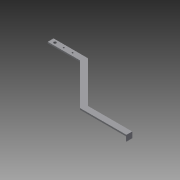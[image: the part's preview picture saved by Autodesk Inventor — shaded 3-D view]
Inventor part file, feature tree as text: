
AUTODESK INVENTOR PART (.ipt)
format: ipt  version: 2013 (Build 170138000, 138)  size: 174,080 bytes
history: native  units: in
note: dims shown in document units (in); Inventor stores cm internally (conversion verified against a paired STEP export)
features: extrude x8, sketch x8
ambient origin geometry x8: Origin, YZ Plane, XZ Plane, XY Plane, X Axis, Y Axis, Z Axis, Center Point
bodies: Solid1 (feature_tree)
feature tree (16):
  extrude  "Extrusion1"  Depth=1.0in
  extrude  "Extrusion2"  Depth=1.0in
  extrude  "Extrusion3"  Depth=9.586in
  extrude  "Extrusion5"  Depth=7.5in
  extrude  "Extrusion7"  Depth=0.25in TaperAngle=0.0deg
  extrude  "Extrusion8"  Depth=1.0in
  extrude  "Extrusion9"  Depth=1.75in TaperAngle=0.0deg
  extrude  "Extrusion10"  Depth=2.25in
  sketch  "Sketch1"  dims[d0=5.25in d1=1.0in]
  sketch  "Sketch2"  dims[d2=112.5deg d3=1.0in]
  sketch  "Sketch3"  dims[d4=135.0deg d5=9.586in]
  sketch  "Sketch6"  dims[d6=0.5in d7=7.5in]
  sketch  "Sketch8"  dims[d8=1.0in d9=0.25in d10=0.0in]
  sketch  "Sketch9"  dims[d11=1.0in d12=1.0in]
  sketch  "Sketch10"  dims[d13=0.0625in d14=0.0in d15=1.75in d16=0.0in]
  sketch  "Sketch11"  dims[d21=0.25in d22=0.0in d29=2.25in d30=1.5in d31=3.0in d32=0.0in d33=0.25in d34=0.25in d35=1.0in d36=0.0in d37=1.75in d38=1.0in d39=1.5in d40=0.0in d41=0.25in d42=1.0in d43=0.0in d44=0.25in d45=0.0in d46=0.25in d47=180.0deg d48=0.25in d49=0.0in]
